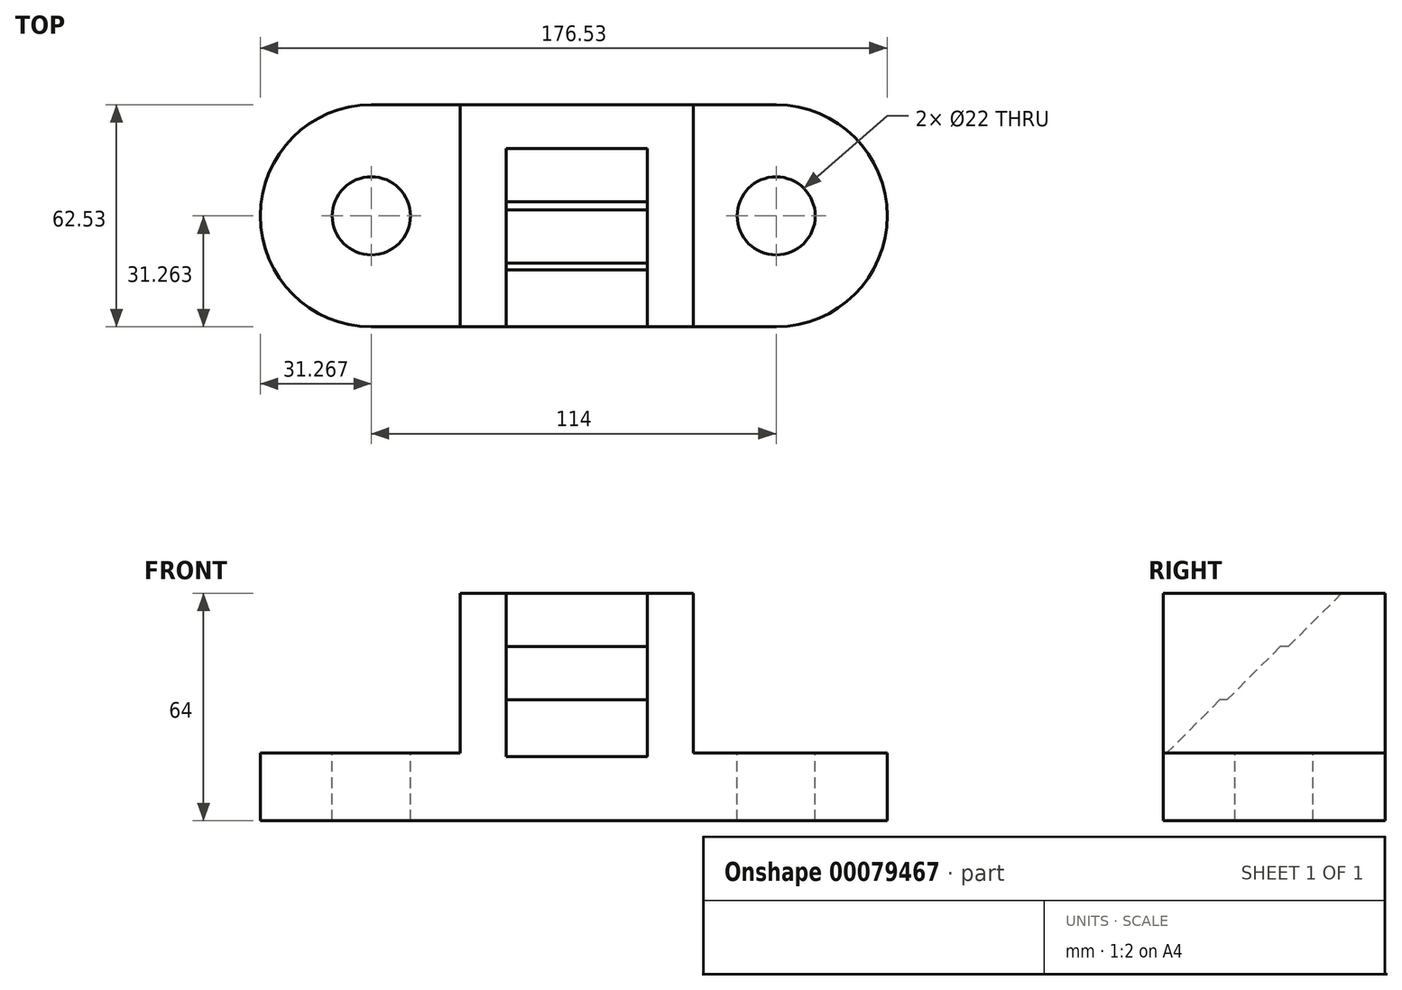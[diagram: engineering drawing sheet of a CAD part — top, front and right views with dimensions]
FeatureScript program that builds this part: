
annotation { "Feature Type Name" : "Feature", "Feature Type Description" : "" }
export const myFeature = defineFeature(function(context is Context, id is Id, definition is map)
    precondition{}
    {
        {
            var Q0;
            Q0=qCreatedBy(makeId("Top.planeOp"),FACE);
            var sketch = newSketch(context, id + "F0", { "sketchPlane" : qUnion([Q0])});
            skLineSegment(sketch, "E0.bottom", {"start": v(-107.87, -7.64) * mm, "end": v(6.13, -7.64) * mm});
            skLineSegment(sketch, "E0.top", {"start": v(-107.87, 54.89) * mm, "end": v(6.13, 54.89) * mm});
            skArc(sketch, "E1", {"start": v(-107.87, 54.89) * mm, "mid": v(-139.14, 23.62) * mm, "end": v(-107.87, -7.64) * mm});
            skArc(sketch, "E2", {"start": v(6.13, 54.89) * mm, "mid": v(37.4, 23.62) * mm, "end": v(6.13, -7.64) * mm});
            skSolve(sketch);
        }
        {
            var Q0;
            Q0 = qSketchRegion(id + "F0", true);
            extrude(context, id + "F1", {"entities" : qUnion([Q0]), "depth" : 19 * mm});
        }
        {
            var Q0;
            Q0=makeQuery(id+"F1.opExtrude","CAP_FACE",FACE,{"disambiguationData":[OSD([sQuery(id+"F0.wireOp",EDGE,"E0.bottom"),sQuery(id+"F0.wireOp",EDGE,"E0.top"),sQuery(id+"F0.wireOp",EDGE,"E1"),sQuery(id+"F0.wireOp",EDGE,"E2")])],"isStart":false});
            var sketch = newSketch(context, id + "F2", { "sketchPlane" : qUnion([Q0])});
            skCircle(sketch, "E3", {"center": v(-107.87, 23.62) * mm, "radius": 11 * mm});
            skCircle(sketch, "E4", {"center": v(6.13, 23.62) * mm, "radius": 11 * mm});
            skSolve(sketch);
        }
        {
            var Q0;
            Q0 = qSketchRegion(id + "F2", true);
            extrude(context, id + "F3", {"entities" : qUnion([Q0]), "operationType" : NewBodyOperationType.REMOVE, "oppositeDirection" : true, "depth" : 19 * mm});
        }
        {
            var Q0;
            Q0=makeQuery(id+"F1.opExtrude","CAP_FACE",FACE,{"disambiguationData":[OSD([sQuery(id+"F0.wireOp",EDGE,"E0.bottom"),sQuery(id+"F0.wireOp",EDGE,"E0.top"),sQuery(id+"F0.wireOp",EDGE,"E1"),sQuery(id+"F0.wireOp",EDGE,"E2")])],"isStart":false});
            var sketch = newSketch(context, id + "F4", { "sketchPlane" : qUnion([Q0])});
            skLineSegment(sketch, "E5", {"start": v(-82.87, 54.89) * mm, "end": v(-82.87, -7.64) * mm});
            skLineSegment(sketch, "E6", {"start": v(-17.18, 54.89) * mm, "end": v(-17.18, -7.64) * mm});
            skLineSegment(sketch, "E7", {"start": v(-82.87, 54.89) * mm, "end": v(-17.18, 54.89) * mm});
            skLineSegment(sketch, "E8", {"start": v(-82.87, -7.64) * mm, "end": v(-69.87, -7.64) * mm});
            skLineSegment(sketch, "E9", {"start": v(-17.18, -7.64) * mm, "end": v(-30.18, -7.64) * mm});
            skLineSegment(sketch, "E10", {"start": v(-69.87, 41.89) * mm, "end": v(-69.87, -7.64) * mm});
            skLineSegment(sketch, "E11", {"start": v(-69.87, 41.89) * mm, "end": v(-30.18, 41.89) * mm});
            skLineSegment(sketch, "E12", {"start": v(-30.18, 41.89) * mm, "end": v(-30.18, -7.64) * mm});
            skSolve(sketch);
        }
        {
            var Q0;
            Q0 = qSketchRegion(id + "F4", true);
            extrude(context, id + "F5", {"entities" : qUnion([Q0]), "operationType" : NewBodyOperationType.ADD, "depth" : 45 * mm});
        }
        {
            var Q0;
            {var subQ0=sQuery(id+"F0.wireOp",EDGE,"E0.bottom");Q0=makeQuery(id+"F5.boolean.opBoolean","SPLIT",FACE,{"disambiguationData":[TD([makeQuery(id+"F5.opExtrude","SWEPT_FACE",FACE,{"disambiguationData":[OSD([sQuery(id+"F4.wireOp",EDGE,"E10")])]})])],"derivedFrom":makeQuery(id+"F1.opExtrude","CAP_FACE",FACE,{"disambiguationData":[OSD([subQ0,sQuery(id+"F0.wireOp",EDGE,"E0.top"),sQuery(id+"F0.wireOp",EDGE,"E1"),sQuery(id+"F0.wireOp",EDGE,"E2")])],"isStart":false})});}
            var sketch = newSketch(context, id + "F6", { "sketchPlane" : qUnion([Q0])});
            skLineSegment(sketch, "E13.bottom", {"start": v(-69.87, -7.64) * mm, "end": v(-30.18, -7.64) * mm});
            skLineSegment(sketch, "E13.top", {"start": v(-69.87, 9.36) * mm, "end": v(-30.18, 9.36) * mm});
            skLineSegment(sketch, "E13.left", {"start": v(-69.87, -7.64) * mm, "end": v(-69.87, 9.36) * mm});
            skLineSegment(sketch, "E13.right", {"start": v(-30.18, -7.64) * mm, "end": v(-30.18, 9.36) * mm});
            skSolve(sketch);
        }
        {
            var Q0;
            Q0 = qSketchRegion(id + "F6", true);
            extrude(context, id + "F7", {"entities" : qUnion([Q0]), "operationType" : NewBodyOperationType.ADD, "depth" : 15 * mm});
        }
        {
            var Q0;
            {var subQ0=sQuery(id+"F0.wireOp",EDGE,"E0.bottom");Q0=makeQuery(id+"F5.boolean.opBoolean","SPLIT",FACE,{"disambiguationData":[TD([makeQuery(id+"F5.opExtrude","SWEPT_FACE",FACE,{"disambiguationData":[OSD([sQuery(id+"F4.wireOp",EDGE,"E10")])]})])],"derivedFrom":makeQuery(id+"F1.opExtrude","CAP_FACE",FACE,{"disambiguationData":[OSD([subQ0,sQuery(id+"F0.wireOp",EDGE,"E0.top"),sQuery(id+"F0.wireOp",EDGE,"E1"),sQuery(id+"F0.wireOp",EDGE,"E2")])],"isStart":false})});}
            var sketch = newSketch(context, id + "F8", { "sketchPlane" : qUnion([Q0])});
            skLineSegment(sketch, "E14.bottom", {"start": v(-69.87, 9.36) * mm, "end": v(-30.18, 9.36) * mm});
            skLineSegment(sketch, "E14.top", {"start": v(-69.87, 25.62) * mm, "end": v(-30.18, 25.62) * mm});
            skLineSegment(sketch, "E14.left", {"start": v(-69.87, 9.36) * mm, "end": v(-69.87, 25.62) * mm});
            skLineSegment(sketch, "E14.right", {"start": v(-30.18, 9.36) * mm, "end": v(-30.18, 25.62) * mm});
            skSolve(sketch);
        }
        {
            var Q0;
            Q0 = qSketchRegion(id + "F8", true);
            extrude(context, id + "F9", {"entities" : qUnion([Q0]), "operationType" : NewBodyOperationType.ADD, "depth" : 30 * mm});
        }
        {
            var Q0;
            Q0=makeQuery(id+"F9.opExtrude","CAP_EDGE",EDGE,{"disambiguationData":[OSD([sQuery(id+"F8.wireOp",EDGE,"E14.bottom")])],"isStart":false});
            var Q1;
            Q1=makeQuery(id+"F7.opExtrude","CAP_EDGE",EDGE,{"disambiguationData":[OSD([sQuery(id+"F6.wireOp",EDGE,"E13.bottom")])],"isStart":false});
            chamfer(context, id + "F10", {"entities" : qUnion([Q0, Q1]), "width" : 16 * mm, "tangentPropagation" : true});
        }
        {
            var Q0;
            {var subQ0=sQuery(id+"F0.wireOp",EDGE,"E0.bottom");Q0=makeQuery(id+"F5.boolean.opBoolean","SPLIT",FACE,{"disambiguationData":[TD([makeQuery(id+"F5.opExtrude","SWEPT_FACE",FACE,{"disambiguationData":[OSD([sQuery(id+"F4.wireOp",EDGE,"E10")])]})])],"derivedFrom":makeQuery(id+"F1.opExtrude","CAP_FACE",FACE,{"disambiguationData":[OSD([subQ0,sQuery(id+"F0.wireOp",EDGE,"E0.top"),sQuery(id+"F0.wireOp",EDGE,"E1"),sQuery(id+"F0.wireOp",EDGE,"E2")])],"isStart":false})});}
            var sketch = newSketch(context, id + "F11", { "sketchPlane" : qUnion([Q0])});
            skLineSegment(sketch, "E15.bottom", {"start": v(-69.87, 41.89) * mm, "end": v(-30.18, 41.89) * mm});
            skLineSegment(sketch, "E15.top", {"start": v(-69.87, 25.62) * mm, "end": v(-30.18, 25.62) * mm});
            skLineSegment(sketch, "E15.left", {"start": v(-69.87, 41.89) * mm, "end": v(-69.87, 25.62) * mm});
            skLineSegment(sketch, "E15.right", {"start": v(-30.18, 41.89) * mm, "end": v(-30.18, 25.62) * mm});
            skSolve(sketch);
        }
        {
            var Q0;
            Q0 = qSketchRegion(id + "F11", true);
            extrude(context, id + "F12", {"entities" : qUnion([Q0]), "operationType" : NewBodyOperationType.ADD, "depth" : 45 * mm});
        }
        {
            var Q0;
            Q0=makeQuery(id+"F12.opExtrude","CAP_EDGE",EDGE,{"disambiguationData":[OSD([sQuery(id+"F11.wireOp",EDGE,"E15.top")])],"isStart":false});
            chamfer(context, id + "F13", {"entities" : qUnion([Q0]), "width" : 17 * mm, "tangentPropagation" : true});
        }
    });
